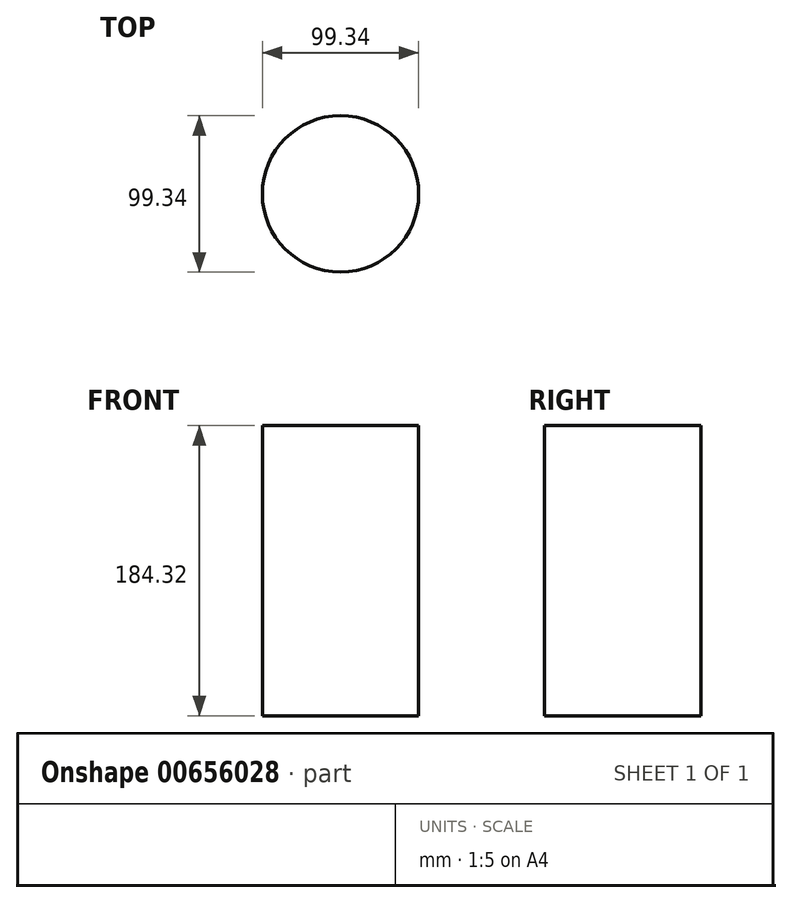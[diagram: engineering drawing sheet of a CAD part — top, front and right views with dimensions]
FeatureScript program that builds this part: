
annotation { "Feature Type Name" : "Feature", "Feature Type Description" : "" }
export const myFeature = defineFeature(function(context is Context, id is Id, definition is map)
    precondition{}
    {
        {
            var Q0;
            Q0=qCreatedBy(makeId("Top.planeOp"),FACE);
            var sketch = newSketch(context, id + "F0", { "sketchPlane" : qUnion([Q0])});
            skCircle(sketch, "E0", {"center": v(0, 0) * mm, "radius": 49.67 * mm});
            skSolve(sketch);
        }
        {
            var Q0;
            Q0=makeQuery(id+"F0.imprint","IMPRINT",FACE,{"disambiguationData":[TD([[makeQuery(id+"F0.imprint","IMPRINT",EDGE,{"derivedFrom":sQuery(id+"F0.wireOp",EDGE,"E0")}),1.0]])]});
            extrude(context, id + "F1", {"entities" : qUnion([Q0]), "depth" : 184.32 * mm, "offsetDistance" : 25.4 * mm});
        }
    });
